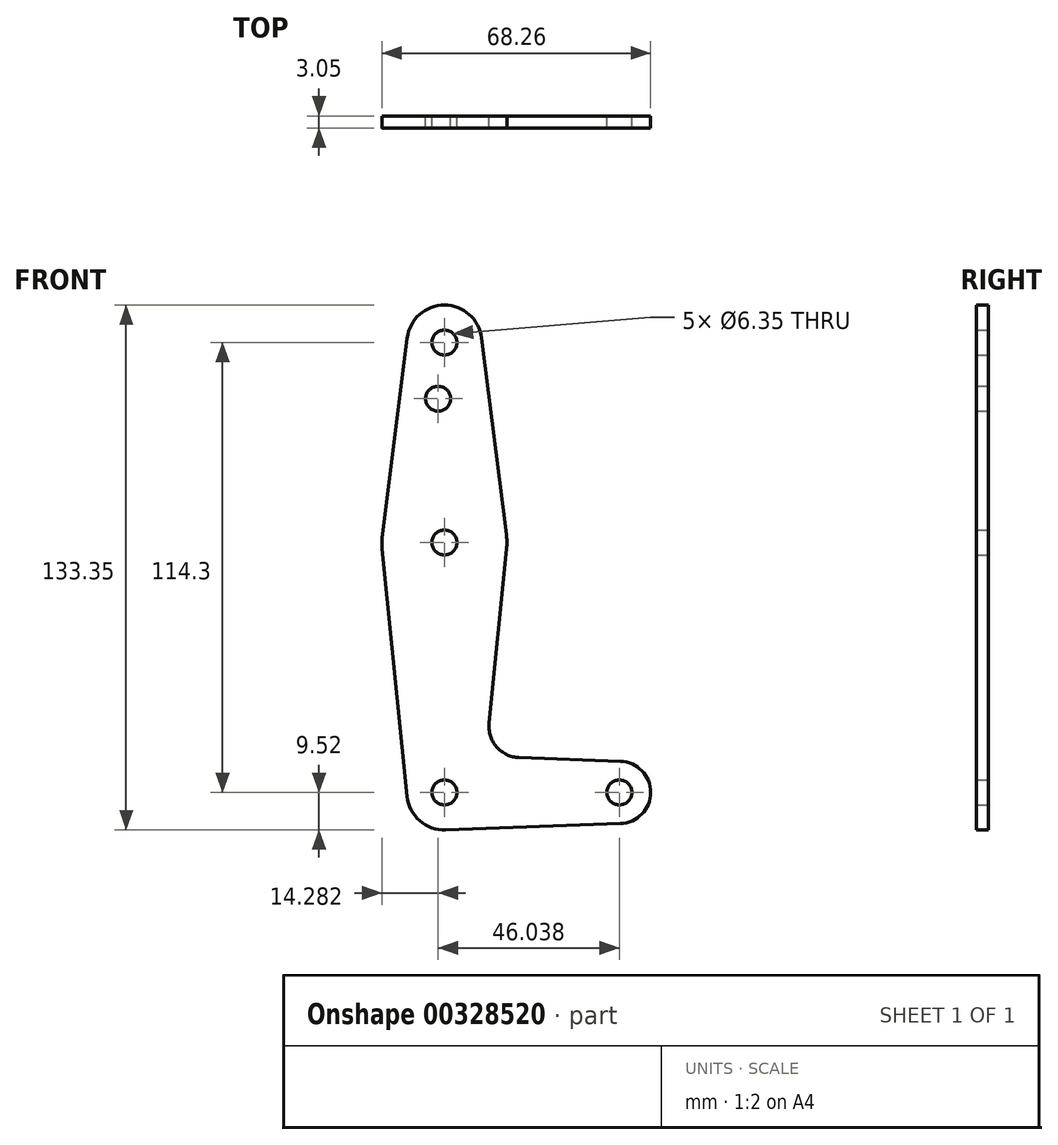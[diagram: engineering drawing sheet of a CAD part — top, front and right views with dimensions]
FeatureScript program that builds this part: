
annotation { "Feature Type Name" : "Feature", "Feature Type Description" : "" }
export const myFeature = defineFeature(function(context is Context, id is Id, definition is map)
    precondition{}
    {
        {
            var Q0;
            Q0=qCreatedBy(makeId("Front.planeOp"),FACE);
            var sketch = newSketch(context, id + "F0", { "sketchPlane" : qUnion([Q0])});
            skLineSegment(sketch, "E0", {"start": v(0, 0) * mm, "end": v(0, 114.3) * mm, "construction": true});
            skLineSegment(sketch, "E1", {"start": v(0, 0) * mm, "end": v(44.45, 0) * mm, "construction": true});
            skCircle(sketch, "E2", {"center": v(0, 114.3) * mm, "radius": 9.53 * mm});
            skCircle(sketch, "E3", {"center": v(0, 0) * mm, "radius": 9.53 * mm});
            skCircle(sketch, "E4", {"center": v(44.45, 0) * mm, "radius": 7.94 * mm});
            skCircle(sketch, "E5", {"center": v(0, 63.5) * mm, "radius": 15.88 * mm});
            skLineSegment(sketch, "E6", {"start": v(9.45, 115.5) * mm, "end": v(15.75, 65.48) * mm});
            skLineSegment(sketch, "E7", {"start": v(-9.45, 115.5) * mm, "end": v(-15.75, 65.48) * mm});
            skLineSegment(sketch, "E8", {"start": v(-15.8, 61.91) * mm, "end": v(-9.48, -0.95) * mm});
            skLineSegment(sketch, "E9", {"start": v(15.8, 61.91) * mm, "end": v(11.34, 17.6) * mm});
            skLineSegment(sketch, "E10", {"start": v(44.73, 7.93) * mm, "end": v(18.97, 8.85) * mm});
            skLineSegment(sketch, "E11", {"start": v(44.73, -7.93) * mm, "end": v(0, -9.53) * mm});
            skCircle(sketch, "E12", {"center": v(0, 114.3) * mm, "radius": 3.18 * mm});
            skCircle(sketch, "E13", {"center": v(0, 0) * mm, "radius": 3.18 * mm});
            skCircle(sketch, "E14", {"center": v(44.45, 0) * mm, "radius": 3.18 * mm});
            skCircle(sketch, "E15", {"center": v(0, 63.5) * mm, "radius": 3.18 * mm});
            skArc(sketch, "E16.filletArc", {"start": v(11.34, 17.6) * mm, "mid": v(13.26, 11.57) * mm, "end": v(18.97, 8.85) * mm});
            skCircle(sketch, "E17", {"center": v(-1.59, 100.03) * mm, "radius": 3.18 * mm});
            skSolve(sketch);
        }
        {
            var Q0;
            Q0 = qSketchRegion(id + "F0", true);
            extrude(context, id + "F1", {"entities" : qUnion([Q0]), "depth" : 3.05 * mm});
        }
    });
